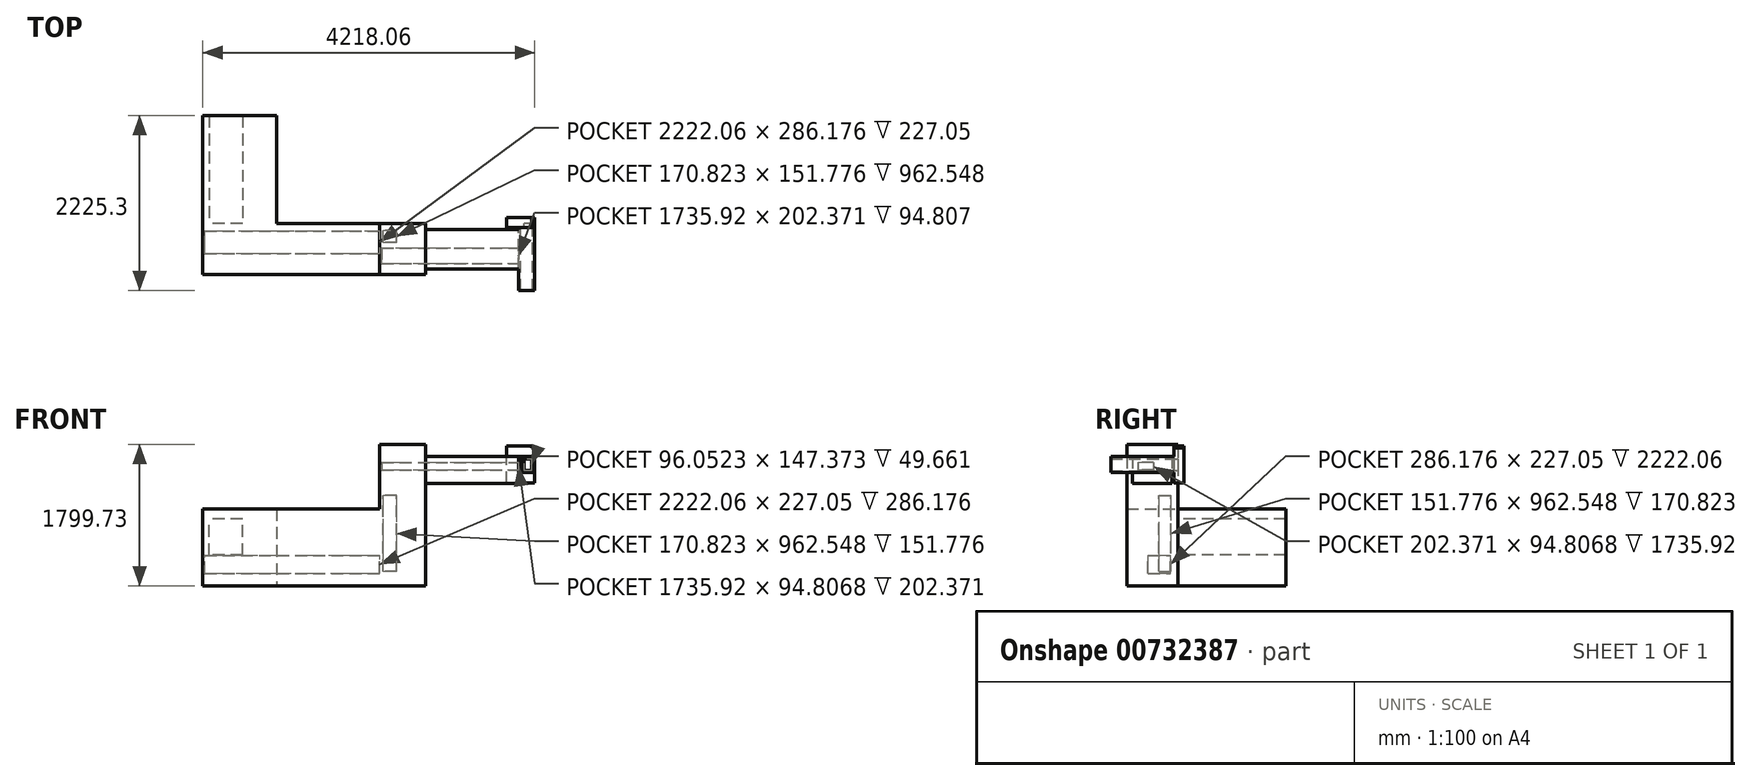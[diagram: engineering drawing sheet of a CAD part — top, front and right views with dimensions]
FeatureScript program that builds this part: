
annotation { "Feature Type Name" : "Feature", "Feature Type Description" : "" }
export const myFeature = defineFeature(function(context is Context, id is Id, definition is map)
    precondition{}
    {
        {
            var Q0;
            Q0=qCreatedBy(makeId("Front.planeOp"),FACE);
            var sketch = newSketch(context, id + "F0", { "sketchPlane" : qUnion([Q0])});
            skLineSegment(sketch, "E0.bottom", {"start": v(-101.43, -98.33) * mm, "end": v(107.84, -98.33) * mm});
            skLineSegment(sketch, "E0.top", {"start": v(-101.43, 103.31) * mm, "end": v(107.84, 103.31) * mm});
            skLineSegment(sketch, "E0.left", {"start": v(-101.43, -98.33) * mm, "end": v(-101.43, 103.31) * mm});
            skLineSegment(sketch, "E0.right", {"start": v(107.84, -98.33) * mm, "end": v(107.84, 103.31) * mm});
            skLineSegment(sketch, "E1.bottom", {"start": v(-74.45, 74.62) * mm, "end": v(76.77, 74.62) * mm});
            skLineSegment(sketch, "E1.top", {"start": v(-74.45, -77.14) * mm, "end": v(76.77, -77.14) * mm});
            skLineSegment(sketch, "E1.left", {"start": v(-74.45, 74.62) * mm, "end": v(-74.45, -77.14) * mm});
            skLineSegment(sketch, "E1.right", {"start": v(76.77, 74.62) * mm, "end": v(76.77, -77.14) * mm});
            skSolve(sketch);
        }
        {
            var Q0;
            Q0 = qSketchRegion(id + "F0", true);
            extrude(context, id + "F1", {"entities" : qUnion([Q0]), "depth" : 930.34 * mm, "offsetDistance" : 25.4 * mm});
        }
        {
            var Q0;
            Q0=makeQuery(id+"F1.opExtrude","CAP_FACE",FACE,{"disambiguationData":[OSD([sQuery(id+"F0.wireOp",EDGE,"E0.bottom"),sQuery(id+"F0.wireOp",EDGE,"E0.top"),sQuery(id+"F0.wireOp",EDGE,"E0.left"),sQuery(id+"F0.wireOp",EDGE,"E0.right"),sQuery(id+"F0.wireOp",EDGE,"E1.bottom"),sQuery(id+"F0.wireOp",EDGE,"E1.top"),sQuery(id+"F0.wireOp",EDGE,"E1.left"),sQuery(id+"F0.wireOp",EDGE,"E1.right")])],"isStart":true});
            var sketch = newSketch(context, id + "F2", { "sketchPlane" : qUnion([Q0])});
            skLineSegment(sketch, "E2.bottom", {"start": v(-107.84, 103.31) * mm, "end": v(27.36, 103.31) * mm});
            skLineSegment(sketch, "E2.top", {"start": v(-107.84, -17.25) * mm, "end": v(27.36, -17.25) * mm});
            skLineSegment(sketch, "E2.left", {"start": v(-107.84, 103.31) * mm, "end": v(-107.84, -17.25) * mm});
            skLineSegment(sketch, "E2.right", {"start": v(27.36, 103.31) * mm, "end": v(27.36, -17.25) * mm});
            skLineSegment(sketch, "E3.bottom", {"start": v(27.36, 103.31) * mm, "end": v(101.43, 103.31) * mm});
            skLineSegment(sketch, "E3.top", {"start": v(27.36, -98.33) * mm, "end": v(101.43, -98.33) * mm});
            skLineSegment(sketch, "E3.left", {"start": v(27.36, 103.31) * mm, "end": v(27.36, -98.33) * mm});
            skLineSegment(sketch, "E3.right", {"start": v(101.43, 103.31) * mm, "end": v(101.43, -98.33) * mm});
            skLineSegment(sketch, "E4.bottom", {"start": v(27.36, -98.33) * mm, "end": v(-107.84, -98.33) * mm});
            skLineSegment(sketch, "E4.top", {"start": v(27.36, -17.25) * mm, "end": v(-107.84, -17.25) * mm});
            skLineSegment(sketch, "E4.left", {"start": v(27.36, -98.33) * mm, "end": v(27.36, -17.25) * mm});
            skLineSegment(sketch, "E4.right", {"start": v(-107.84, -98.33) * mm, "end": v(-107.84, -17.25) * mm});
            skLineSegment(sketch, "E5.bottom", {"start": v(121.24, -121.47) * mm, "end": v(-107.63, -121.47) * mm});
            skLineSegment(sketch, "E5.top", {"start": v(121.24, 126.57) * mm, "end": v(-107.63, 126.57) * mm});
            skLineSegment(sketch, "E5.left", {"start": v(121.24, -121.47) * mm, "end": v(121.24, 126.57) * mm});
            skLineSegment(sketch, "E5.right", {"start": v(-107.63, -121.47) * mm, "end": v(-107.63, 126.57) * mm});
            skSolve(sketch);
        }
        {
            var Q0;
            Q0 = qSketchRegion(id + "F2", true);
            extrude(context, id + "F3", {"entities" : qUnion([Q0]), "operationType" : NewBodyOperationType.ADD, "oppositeDirection" : true, "depth" : 77.62 * mm, "offsetDistance" : 25.4 * mm});
        }
        {
            var Q0;
            Q0=makeQuery(id+"F3.boolean.opBoolean","MERGE",FACE,{"derivedFrom":[makeQuery(id+"F1.opExtrude","CAP_FACE",FACE,{"disambiguationData":[OSD([sQuery(id+"F0.wireOp",EDGE,"E0.bottom"),sQuery(id+"F0.wireOp",EDGE,"E0.top"),sQuery(id+"F0.wireOp",EDGE,"E0.left"),sQuery(id+"F0.wireOp",EDGE,"E0.right"),sQuery(id+"F0.wireOp",EDGE,"E1.bottom"),sQuery(id+"F0.wireOp",EDGE,"E1.top"),sQuery(id+"F0.wireOp",EDGE,"E1.left"),sQuery(id+"F0.wireOp",EDGE,"E1.right")])],"isStart":true}),makeQuery(id+"F3.opExtrude","CAP_FACE",FACE,{"disambiguationData":[OSD([sQuery(id+"F2.wireOp",EDGE,"E2.bottom"),sQuery(id+"F2.wireOp",EDGE,"E2.left"),sQuery(id+"F2.wireOp",EDGE,"E3.bottom"),sQuery(id+"F2.wireOp",EDGE,"E3.top"),sQuery(id+"F2.wireOp",EDGE,"E3.left"),sQuery(id+"F2.wireOp",EDGE,"E3.right"),sQuery(id+"F2.wireOp",EDGE,"E4.bottom"),sQuery(id+"F2.wireOp",EDGE,"E4.left"),sQuery(id+"F2.wireOp",EDGE,"E4.right"),sQuery(id+"F2.wireOp",EDGE,"E5.bottom"),sQuery(id+"F2.wireOp",EDGE,"E5.top"),sQuery(id+"F2.wireOp",EDGE,"E5.left"),sQuery(id+"F2.wireOp",EDGE,"E5.right")])],"isStart":true})]});
            var sketch = newSketch(context, id + "F4", { "sketchPlane" : qUnion([Q0])});
            skLineSegment(sketch, "E6.bottom", {"start": v(27.36, 74.62) * mm, "end": v(-68.7, 74.62) * mm});
            skLineSegment(sketch, "E6.top", {"start": v(27.36, -72.75) * mm, "end": v(-68.7, -72.75) * mm});
            skLineSegment(sketch, "E6.left", {"start": v(27.36, 74.62) * mm, "end": v(27.36, -72.75) * mm});
            skLineSegment(sketch, "E6.right", {"start": v(-68.7, 74.62) * mm, "end": v(-68.7, -72.75) * mm});
            skPoint(sketch, "E7.oppositeSnap0", {"position": v(-68.7, 0.93) * mm});
            skLineSegment(sketch, "E7.bottom", {"start": v(249.8, -234.84) * mm, "end": v(-68.7, -234.84) * mm});
            skLineSegment(sketch, "E7.top", {"start": v(249.8, 234.38) * mm, "end": v(-68.7, 234.38) * mm});
            skLineSegment(sketch, "E7.left", {"start": v(249.8, -234.84) * mm, "end": v(249.8, 234.38) * mm});
            skLineSegment(sketch, "E7.right", {"start": v(-68.7, -234.84) * mm, "end": v(-68.7, 234.38) * mm});
            skLineSegment(sketch, "E8.bottom", {"start": v(-51.05, -234.84) * mm, "end": v(-107.84, -234.84) * mm});
            skLineSegment(sketch, "E8.top", {"start": v(-51.05, 214.01) * mm, "end": v(-107.84, 214.01) * mm});
            skLineSegment(sketch, "E8.left", {"start": v(-51.05, -234.84) * mm, "end": v(-51.05, 214.01) * mm});
            skLineSegment(sketch, "E8.right", {"start": v(-107.84, -234.84) * mm, "end": v(-107.84, 214.01) * mm});
            skSolve(sketch);
        }
        {
            var Q0;
            Q0 = qSketchRegion(id + "F4", true);
            extrude(context, id + "F5", {"entities" : qUnion([Q0]), "operationType" : NewBodyOperationType.ADD, "oppositeDirection" : true, "depth" : 127.28 * mm, "offsetDistance" : 25.4 * mm});
        }
        {
            var Q0;
            Q0=makeQuery(id+"F1.opExtrude","SWEPT_FACE",FACE,{"disambiguationData":[OSD([sQuery(id+"F0.wireOp",EDGE,"E0.left")])]});
            var sketch = newSketch(context, id + "F6", { "sketchPlane" : qUnion([Q0])});
            skLineSegment(sketch, "E9.bottom", {"start": v(384.87, 26.8) * mm, "end": v(587.24, 26.8) * mm});
            skLineSegment(sketch, "E9.top", {"start": v(384.87, -68.02) * mm, "end": v(587.24, -68.02) * mm});
            skLineSegment(sketch, "E9.left", {"start": v(384.87, 26.8) * mm, "end": v(384.87, -68.02) * mm});
            skLineSegment(sketch, "E9.right", {"start": v(587.24, 26.8) * mm, "end": v(587.24, -68.02) * mm});
            skLineSegment(sketch, "E10.bottom", {"start": v(151.97, 103.31) * mm, "end": v(655.32, 103.31) * mm});
            skLineSegment(sketch, "E10.top", {"start": v(151.97, -241.28) * mm, "end": v(655.32, -241.28) * mm});
            skLineSegment(sketch, "E10.left", {"start": v(151.97, 103.31) * mm, "end": v(151.97, -241.28) * mm});
            skLineSegment(sketch, "E10.right", {"start": v(655.32, 103.31) * mm, "end": v(655.32, -241.28) * mm});
            skSolve(sketch);
        }
        {
            var Q0;
            Q0 = qSketchRegion(id + "F6", true);
            extrude(context, id + "F7", {"entities" : qUnion([Q0]), "operationType" : NewBodyOperationType.ADD, "depth" : 1179.8 * mm, "offsetDistance" : 25.4 * mm});
        }
        {
            var Q0;
            Q0=makeQuery(id+"F7.opExtrude","CAP_FACE",FACE,{"disambiguationData":[OSD([sQuery(id+"F6.wireOp",EDGE,"E9.bottom"),sQuery(id+"F6.wireOp",EDGE,"E9.top"),sQuery(id+"F6.wireOp",EDGE,"E9.left"),sQuery(id+"F6.wireOp",EDGE,"E9.right"),sQuery(id+"F6.wireOp",EDGE,"E10.bottom"),sQuery(id+"F6.wireOp",EDGE,"E10.top"),sQuery(id+"F6.wireOp",EDGE,"E10.left"),sQuery(id+"F6.wireOp",EDGE,"E10.right")])],"isStart":false});
            var sketch = newSketch(context, id + "F8", { "sketchPlane" : qUnion([Q0])});
            skLineSegment(sketch, "E11.bottom", {"start": v(726.73, 259.17) * mm, "end": v(74.65, 259.17) * mm});
            skLineSegment(sketch, "E11.top", {"start": v(726.73, -392.43) * mm, "end": v(74.65, -392.43) * mm});
            skLineSegment(sketch, "E11.left", {"start": v(726.73, 259.17) * mm, "end": v(726.73, -392.43) * mm});
            skLineSegment(sketch, "E11.right", {"start": v(74.65, 259.17) * mm, "end": v(74.65, -392.43) * mm});
            skLineSegment(sketch, "E12.bottom", {"start": v(587.24, -68.02) * mm, "end": v(384.87, -68.02) * mm});
            skLineSegment(sketch, "E12.top", {"start": v(587.24, 26.8) * mm, "end": v(384.87, 26.8) * mm});
            skLineSegment(sketch, "E12.left", {"start": v(587.24, -68.02) * mm, "end": v(587.24, 26.8) * mm});
            skLineSegment(sketch, "E12.right", {"start": v(384.87, -68.02) * mm, "end": v(384.87, 26.8) * mm});
            skSolve(sketch);
        }
        {
            var Q0;
            Q0 = qSketchRegion(id + "F8", true);
            extrude(context, id + "F9", {"entities" : qUnion([Q0]), "operationType" : NewBodyOperationType.ADD, "depth" : 556.12 * mm, "offsetDistance" : 25.4 * mm});
        }
        {
            var Q0;
            Q0=makeQuery(id+"F9.opExtrude","CAP_FACE",FACE,{"disambiguationData":[OSD([sQuery(id+"F8.wireOp",EDGE,"E11.bottom"),sQuery(id+"F8.wireOp",EDGE,"E11.top"),sQuery(id+"F8.wireOp",EDGE,"E11.left"),sQuery(id+"F8.wireOp",EDGE,"E11.right"),sQuery(id+"F8.wireOp",EDGE,"E12.bottom"),sQuery(id+"F8.wireOp",EDGE,"E12.top"),sQuery(id+"F8.wireOp",EDGE,"E12.left"),sQuery(id+"F8.wireOp",EDGE,"E12.right")])],"isStart":false});
            var sketch = newSketch(context, id + "F10", { "sketchPlane" : qUnion([Q0])});
            skLineSegment(sketch, "E13.bottom", {"start": v(587.24, -20.61) * mm, "end": v(726.73, -20.61) * mm});
            skLineSegment(sketch, "E13.top", {"start": v(587.24, 259.17) * mm, "end": v(726.73, 259.17) * mm});
            skLineSegment(sketch, "E13.left", {"start": v(587.24, -20.61) * mm, "end": v(587.24, 259.17) * mm});
            skLineSegment(sketch, "E13.right", {"start": v(726.73, -20.61) * mm, "end": v(726.73, 259.17) * mm});
            skLineSegment(sketch, "E14.top", {"start": v(587.24, -392.43) * mm, "end": v(726.73, -392.43) * mm});
            skLineSegment(sketch, "E14.left", {"start": v(587.24, 259.17) * mm, "end": v(587.24, -392.43) * mm});
            skLineSegment(sketch, "E14.right", {"start": v(726.73, 259.17) * mm, "end": v(726.73, -392.43) * mm});
            skLineSegment(sketch, "E15.bottom", {"start": v(587.24, -392.43) * mm, "end": v(74.65, -392.43) * mm});
            skLineSegment(sketch, "E15.top", {"start": v(587.24, 259.17) * mm, "end": v(74.65, 259.17) * mm});
            skLineSegment(sketch, "E15.left", {"start": v(587.24, -392.43) * mm, "end": v(587.24, 259.17) * mm});
            skLineSegment(sketch, "E15.right", {"start": v(74.65, -392.43) * mm, "end": v(74.65, 259.17) * mm});
            skSolve(sketch);
        }
        {
            var Q0;
            Q0 = qSketchRegion(id + "F10", true);
            extrude(context, id + "F11", {"entities" : qUnion([Q0]), "operationType" : NewBodyOperationType.ADD, "depth" : 25.4 * mm, "offsetDistance" : 25.4 * mm});
        }
        {
            var Q0;
            Q0=makeQuery(id+"F11.boolean.opBoolean","MERGE",FACE,{"derivedFrom":[makeQuery(id+"F9.opExtrude","SWEPT_FACE",FACE,{"disambiguationData":[OSD([sQuery(id+"F8.wireOp",EDGE,"E11.top")])]}),makeQuery(id+"F11.opExtrude","SWEPT_FACE",FACE,{"disambiguationData":[OSD([sQuery(id+"F10.wireOp",EDGE,"E14.top"),sQuery(id+"F10.wireOp",EDGE,"E15.bottom")])]})]});
            var sketch = newSketch(context, id + "F12", { "sketchPlane" : qUnion([Q0])});
            skLineSegment(sketch, "E16.bottom", {"start": v(-1646.04, 315.58) * mm, "end": v(-1816.86, 315.58) * mm});
            skLineSegment(sketch, "E16.top", {"start": v(-1646.04, 163.8) * mm, "end": v(-1816.86, 163.8) * mm});
            skLineSegment(sketch, "E16.left", {"start": v(-1646.04, 315.58) * mm, "end": v(-1646.04, 163.8) * mm});
            skLineSegment(sketch, "E16.right", {"start": v(-1816.86, 315.58) * mm, "end": v(-1816.86, 163.8) * mm});
            skLineSegment(sketch, "E17.bottom", {"start": v(-1862.75, 726.73) * mm, "end": v(-1281.24, 726.73) * mm});
            skLineSegment(sketch, "E17.top", {"start": v(-1862.75, 74.65) * mm, "end": v(-1281.24, 74.65) * mm});
            skLineSegment(sketch, "E17.left", {"start": v(-1862.75, 726.73) * mm, "end": v(-1862.75, 74.65) * mm});
            skLineSegment(sketch, "E17.right", {"start": v(-1281.24, 726.73) * mm, "end": v(-1281.24, 74.65) * mm});
            skSolve(sketch);
        }
        {
            var Q0;
            Q0 = qSketchRegion(id + "F12", true);
            extrude(context, id + "F13", {"entities" : qUnion([Q0]), "operationType" : NewBodyOperationType.ADD, "depth" : 962.55 * mm, "offsetDistance" : 25.4 * mm});
        }
        {
            var Q0;
            Q0=makeQuery(id+"F13.opExtrude","CAP_FACE",FACE,{"disambiguationData":[OSD([sQuery(id+"F12.wireOp",EDGE,"E16.bottom"),sQuery(id+"F12.wireOp",EDGE,"E16.top"),sQuery(id+"F12.wireOp",EDGE,"E16.left"),sQuery(id+"F12.wireOp",EDGE,"E16.right"),sQuery(id+"F12.wireOp",EDGE,"E17.bottom"),sQuery(id+"F12.wireOp",EDGE,"E17.top"),sQuery(id+"F12.wireOp",EDGE,"E17.left"),sQuery(id+"F12.wireOp",EDGE,"E17.right")])],"isStart":false});
            var sketch = newSketch(context, id + "F14", { "sketchPlane" : qUnion([Q0])});
            skLineSegment(sketch, "E18.bottom", {"start": v(-1862.75, 74.65) * mm, "end": v(-1281.24, 74.65) * mm});
            skLineSegment(sketch, "E18.top", {"start": v(-1862.75, 726.73) * mm, "end": v(-1281.24, 726.73) * mm});
            skLineSegment(sketch, "E18.left", {"start": v(-1862.75, 74.65) * mm, "end": v(-1862.75, 726.73) * mm});
            skLineSegment(sketch, "E18.right", {"start": v(-1281.24, 74.65) * mm, "end": v(-1281.24, 726.73) * mm});
            skSolve(sketch);
        }
        {
            var Q0;
            Q0 = qSketchRegion(id + "F14", true);
            extrude(context, id + "F15", {"entities" : qUnion([Q0]), "operationType" : NewBodyOperationType.ADD, "depth" : 185.58 * mm, "offsetDistance" : 25.4 * mm});
        }
        {
            var Q0;
            Q0=makeQuery(id+"F15.boolean.opBoolean","MERGE",FACE,{"derivedFrom":[makeQuery(id+"F13.boolean.opBoolean","MERGE",FACE,{"derivedFrom":[makeQuery(id+"F11.opExtrude","CAP_FACE",FACE,{"disambiguationData":[OSD([sQuery(id+"F10.wireOp",EDGE,"E13.top"),sQuery(id+"F10.wireOp",EDGE,"E14.top"),sQuery(id+"F10.wireOp",EDGE,"E14.right"),sQuery(id+"F10.wireOp",EDGE,"E15.bottom"),sQuery(id+"F10.wireOp",EDGE,"E15.top"),sQuery(id+"F10.wireOp",EDGE,"E15.right")])],"isStart":false}),makeQuery(id+"F13.opExtrude","SWEPT_FACE",FACE,{"disambiguationData":[OSD([sQuery(id+"F12.wireOp",EDGE,"E17.left")])]})]}),makeQuery(id+"F15.opExtrude","SWEPT_FACE",FACE,{"disambiguationData":[OSD([sQuery(id+"F14.wireOp",EDGE,"E18.left")])]})]});
            var sketch = newSketch(context, id + "F16", { "sketchPlane" : qUnion([Q0])});
            skLineSegment(sketch, "E19.bottom", {"start": v(455.84, -1380.47) * mm, "end": v(169.66, -1380.47) * mm});
            skLineSegment(sketch, "E19.top", {"start": v(455.84, -1153.42) * mm, "end": v(169.66, -1153.42) * mm});
            skLineSegment(sketch, "E19.left", {"start": v(455.84, -1380.47) * mm, "end": v(455.84, -1153.42) * mm});
            skLineSegment(sketch, "E19.right", {"start": v(169.66, -1380.47) * mm, "end": v(169.66, -1153.42) * mm});
            skLineSegment(sketch, "E20.bottom", {"start": v(726.73, -1540.56) * mm, "end": v(74.65, -1540.56) * mm});
            skLineSegment(sketch, "E20.top", {"start": v(726.73, -562.62) * mm, "end": v(74.65, -562.62) * mm});
            skLineSegment(sketch, "E20.left", {"start": v(726.73, -1540.56) * mm, "end": v(726.73, -562.62) * mm});
            skLineSegment(sketch, "E20.right", {"start": v(74.65, -1540.56) * mm, "end": v(74.65, -562.62) * mm});
            skSolve(sketch);
        }
        {
            var Q0;
            Q0 = qSketchRegion(id + "F16", true);
            extrude(context, id + "F17", {"entities" : qUnion([Q0]), "operationType" : NewBodyOperationType.ADD, "depth" : 2222.06 * mm, "offsetDistance" : 25.4 * mm});
        }
        {
            var Q0;
            Q0=makeQuery(id+"F17.opExtrude","CAP_FACE",FACE,{"disambiguationData":[OSD([sQuery(id+"F16.wireOp",EDGE,"E19.bottom"),sQuery(id+"F16.wireOp",EDGE,"E19.top"),sQuery(id+"F16.wireOp",EDGE,"E19.left"),sQuery(id+"F16.wireOp",EDGE,"E19.right"),sQuery(id+"F16.wireOp",EDGE,"E20.bottom"),sQuery(id+"F16.wireOp",EDGE,"E20.top"),sQuery(id+"F16.wireOp",EDGE,"E20.left"),sQuery(id+"F16.wireOp",EDGE,"E20.right")])],"isStart":false});
            var sketch = newSketch(context, id + "F18", { "sketchPlane" : qUnion([Q0])});
            skLineSegment(sketch, "E21.bottom", {"start": v(74.65, -1540.56) * mm, "end": v(726.73, -1540.56) * mm});
            skLineSegment(sketch, "E21.top", {"start": v(74.65, -562.62) * mm, "end": v(726.73, -562.62) * mm});
            skLineSegment(sketch, "E21.left", {"start": v(74.65, -1540.56) * mm, "end": v(74.65, -562.62) * mm});
            skLineSegment(sketch, "E21.right", {"start": v(726.73, -1540.56) * mm, "end": v(726.73, -562.62) * mm});
            skSolve(sketch);
        }
        {
            var Q0;
            Q0 = qSketchRegion(id + "F18", true);
            extrude(context, id + "F19", {"entities" : qUnion([Q0]), "operationType" : NewBodyOperationType.ADD, "depth" : 25.4 * mm, "offsetDistance" : 25.4 * mm});
        }
        {
            var Q0;
            Q0=makeQuery(id+"F19.boolean.opBoolean","MERGE",FACE,{"derivedFrom":[makeQuery(id+"F17.boolean.opBoolean","MERGE",FACE,{"derivedFrom":[makeQuery(id+"F15.boolean.opBoolean","MERGE",FACE,{"derivedFrom":[makeQuery(id+"F13.boolean.opBoolean","MERGE",FACE,{"derivedFrom":[makeQuery(id+"F11.boolean.opBoolean","MERGE",FACE,{"derivedFrom":[makeQuery(id+"F9.opExtrude","SWEPT_FACE",FACE,{"disambiguationData":[OSD([sQuery(id+"F8.wireOp",EDGE,"E11.right")])]}),makeQuery(id+"F11.opExtrude","SWEPT_FACE",FACE,{"disambiguationData":[OSD([sQuery(id+"F10.wireOp",EDGE,"E15.right")])]})]}),makeQuery(id+"F13.opExtrude","SWEPT_FACE",FACE,{"disambiguationData":[OSD([sQuery(id+"F12.wireOp",EDGE,"E17.top")])]})]}),makeQuery(id+"F15.opExtrude","SWEPT_FACE",FACE,{"disambiguationData":[OSD([sQuery(id+"F14.wireOp",EDGE,"E18.bottom")])]})]}),makeQuery(id+"F17.opExtrude","SWEPT_FACE",FACE,{"disambiguationData":[OSD([sQuery(id+"F16.wireOp",EDGE,"E20.right")])]})]}),makeQuery(id+"F19.opExtrude","SWEPT_FACE",FACE,{"disambiguationData":[OSD([sQuery(id+"F18.wireOp",EDGE,"E21.left")])]})]});
            var sketch = newSketch(context, id + "F20", { "sketchPlane" : qUnion([Q0])});
            skLineSegment(sketch, "E22.bottom", {"start": v(3604.6, -1147.8) * mm, "end": v(4026.08, -1147.8) * mm});
            skLineSegment(sketch, "E22.top", {"start": v(3604.6, -688.38) * mm, "end": v(4026.08, -688.38) * mm});
            skLineSegment(sketch, "E22.left", {"start": v(3604.6, -1147.8) * mm, "end": v(3604.6, -688.38) * mm});
            skLineSegment(sketch, "E22.right", {"start": v(4026.08, -1147.8) * mm, "end": v(4026.08, -688.38) * mm});
            skLineSegment(sketch, "E23.bottom", {"start": v(4110.22, -562.62) * mm, "end": v(3170.26, -562.62) * mm});
            skLineSegment(sketch, "E23.top", {"start": v(4110.22, -1540.56) * mm, "end": v(3170.26, -1540.56) * mm});
            skLineSegment(sketch, "E23.left", {"start": v(4110.22, -562.62) * mm, "end": v(4110.22, -1540.56) * mm});
            skLineSegment(sketch, "E23.right", {"start": v(3170.26, -562.62) * mm, "end": v(3170.26, -1540.56) * mm});
            skSolve(sketch);
        }
        {
            var Q0;
            Q0 = qSketchRegion(id + "F20", true);
            extrude(context, id + "F21", {"entities" : qUnion([Q0]), "operationType" : NewBodyOperationType.ADD, "depth" : 1369.6 * mm, "offsetDistance" : 25.4 * mm});
        }
    });
